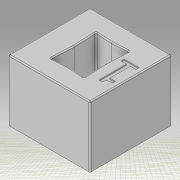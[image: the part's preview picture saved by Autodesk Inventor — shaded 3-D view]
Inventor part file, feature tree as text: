
AUTODESK INVENTOR PART (.ipt)
format: ipt  version: 2018 (Build 220112000, 112)  size: 205,312 bytes
history: native  units: in
note: dims shown in document units (in); Inventor stores cm internally (conversion verified against a paired STEP export)
features: extrude x5, sketch x5, plane x2, mirror x2, fillet x2, projected_geometry x2
ambient origin geometry x8: Origin, YZ Plane, XZ Plane, XY Plane, X Axis, Y Axis, Z Axis, Center Point
bodies: Solid1 (feature_tree)
feature tree (18):
  extrude  "Extrusion1"  Depth=2.0in
  extrude  "Extrusion2"  Depth=0.525in
  extrude  "Extrusion3"  Depth=1.05in
  plane  "Work Plane1"
  plane  "Work Plane2"
  mirror  "Mirror1"
  mirror  "Mirror2"
  fillet  "Fillet1"  Radius=0.941in
  fillet  "Fillet2"  Radius=0.05in
  extrude  "Extrusion4"  Depth=0.05in
  extrude  "Extrusion5"  Depth=0.941in TaperAngle=0.0deg
  sketch  "Sketch1"  dims[d0=2.0in d1=2.0in]
  sketch  "Sketch2"  dims[d2=1.5in d3=0.0in d5=0.525in]
  projected_geometry  "Projected Loop1"
  sketch  "Sketch3"  dims[d6=0.755in d7=1.05in d8=0.941in d9=0.0in d10=0.05in]
  sketch  "Sketch4"  dims[d11=0.05in d12=0.05in]
  sketch  "Sketch5"  dims[d13=0.05in d14=0.941in d15=0.0in d16=0.025in d17=0.025in d18=0.025in d19=0.0in d20=0.515in d21=1.0in d22=0.0in]
  projected_geometry  "Projected Loop2"
